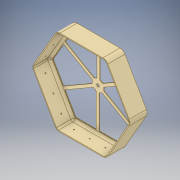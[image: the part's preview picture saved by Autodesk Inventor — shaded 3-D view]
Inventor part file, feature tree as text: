
AUTODESK INVENTOR PART (.ipt)
format: ipt  version: 2019 (Build 230136000, 136)  size: 317,952 bytes
history: native  units: mm
features: mirror x4, extrude x3, sketch x3, plane x3, fillet x3, projected_geometry x2, shell x1
ambient origin geometry x8: Origin, YZ Plane, XZ Plane, XY Plane, X Axis, Y Axis, Z Axis, Center Point
bodies: Solid1 (feature_tree)
feature tree (19):
  extrude  "Extrusion1"  Depth=30.0mm TaperAngle=0.0deg
  shell  "Shell1"  Thickness=1.5mm
  sketch  "Sketch2"  dims[d5=2.0mm d6=15.0mm]
  plane  "Work Plane1"
  plane  "Work Plane2"
  plane  "Work Plane3"
  extrude  "Extrusion5"  Depth=2.0mm
  extrude  "Extrusion2"  Depth=1.0mm TaperAngle=0.0deg
  mirror  "Mirror1"
  mirror  "Mirror2"
  mirror  "Mirror3"
  mirror  "Mirror4"
  fillet  "Fillet1"  Radius=4.0mm
  fillet  "Fillet2"  Radius=10.0mm
  fillet  "Fillet4"  Radius=1.0mm
  sketch  "Sketch1"  dims[d0=150.0mm d2=30.0mm d3=0.0mm d4=1.5mm]
  projected_geometry  "Projected Loop1"
  sketch  "Sketch4"  dims[d7=15.0mm d8=1.0mm d9=0.0mm d10=4.0mm d11=10.0mm d12=1.0mm d37=5.0mm d44=10.0mm d45=60.0deg d46=90.0deg d47=90.0deg d48=60.0mm d50=360.0deg d52=5.5mm d53=10.0mm d54=0.0mm d55=5.0mm d56=2.0mm]
  projected_geometry  "Projected Loop3"
